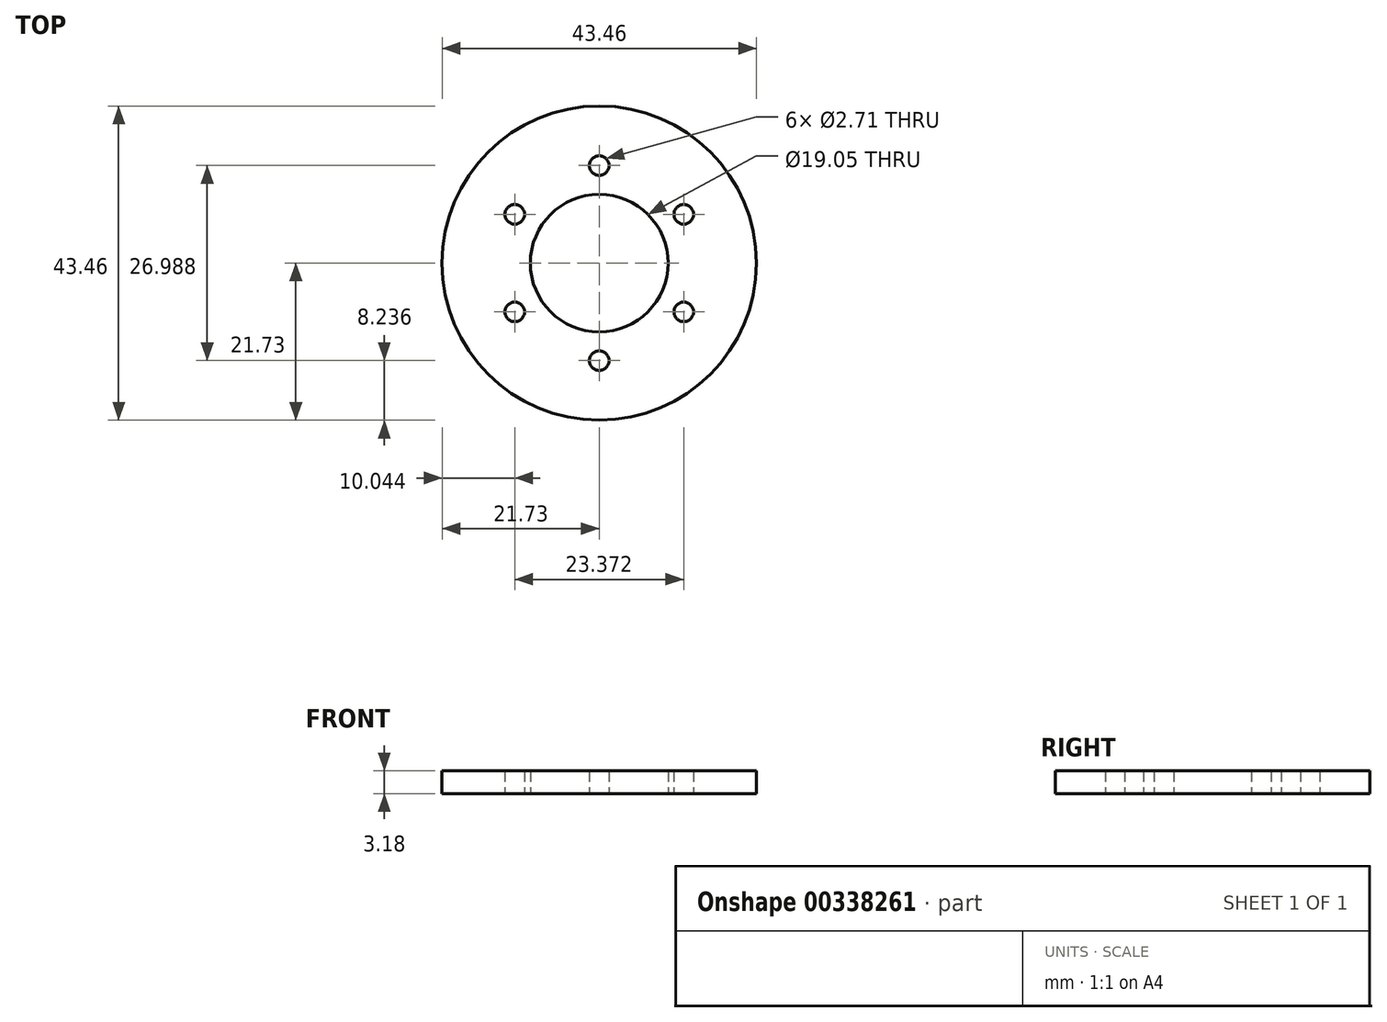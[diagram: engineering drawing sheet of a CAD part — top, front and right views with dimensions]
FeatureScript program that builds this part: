
annotation { "Feature Type Name" : "Feature", "Feature Type Description" : "" }
export const myFeature = defineFeature(function(context is Context, id is Id, definition is map)
    precondition{}
    {
        {
            var Q0;
            Q0=qCreatedBy(makeId("Top.planeOp"),FACE);
            var sketch = newSketch(context, id + "F0", { "sketchPlane" : qUnion([Q0])});
            skCircle(sketch, "E0", {"center": v(0, 0) * mm, "radius": 9.52 * mm});
            skCircle(sketch, "E1", {"center": v(0, 0) * mm, "radius": 21.73 * mm});
            skLineSegment(sketch, "E2", {"start": v(0, 0) * mm, "end": v(0, -13.5) * mm, "construction": true});
            skLineSegment(sketch, "E3", {"start": v(0, -13.5) * mm, "end": v(11.69, 6.75) * mm, "construction": true});
            skLineSegment(sketch, "E4", {"start": v(11.69, 6.75) * mm, "end": v(0, 0) * mm, "construction": true});
            skLineSegment(sketch, "E5", {"start": v(0, 0) * mm, "end": v(-11.69, 6.75) * mm, "construction": true});
            skLineSegment(sketch, "E6", {"start": v(-11.69, 6.75) * mm, "end": v(0, -13.5) * mm, "construction": true});
            skLineSegment(sketch, "E7", {"start": v(-11.69, 6.75) * mm, "end": v(11.69, 6.75) * mm, "construction": true});
            skCircle(sketch, "E8", {"center": v(0, -13.5) * mm, "radius": 3.97 * mm, "construction": true});
            skCircle(sketch, "E9", {"center": v(-11.69, 6.75) * mm, "radius": 1.35 * mm});
            skCircle(sketch, "E10", {"center": v(11.69, 6.75) * mm, "radius": 1.35 * mm});
            skCircle(sketch, "E11", {"center": v(0, -13.5) * mm, "radius": 1.35 * mm});
            skLineSegment(sketch, "E12", {"start": v(0, 0) * mm, "end": v(0, 13.5) * mm, "construction": true});
            skLineSegment(sketch, "E13", {"start": v(0, 13.5) * mm, "end": v(11.69, -6.75) * mm, "construction": true});
            skLineSegment(sketch, "E14", {"start": v(11.69, -6.75) * mm, "end": v(0, 0) * mm, "construction": true});
            skLineSegment(sketch, "E15", {"start": v(0, 0) * mm, "end": v(-11.69, -6.75) * mm, "construction": true});
            skLineSegment(sketch, "E16", {"start": v(-11.69, -6.75) * mm, "end": v(0, 13.5) * mm, "construction": true});
            skLineSegment(sketch, "E17", {"start": v(-11.69, -6.75) * mm, "end": v(11.69, -6.75) * mm, "construction": true});
            skCircle(sketch, "E18", {"center": v(-11.69, -6.75) * mm, "radius": 1.35 * mm});
            skCircle(sketch, "E19", {"center": v(11.69, -6.75) * mm, "radius": 1.35 * mm});
            skCircle(sketch, "E20", {"center": v(0, 13.5) * mm, "radius": 1.35 * mm});
            skSolve(sketch);
        }
        {
            var Q0;
            Q0=qSketchRegion(id+"F0",true);
            extrude(context, id + "F1", {"entities" : qUnion([Q0]), "depth" : 3.17 * mm});
        }
    });
